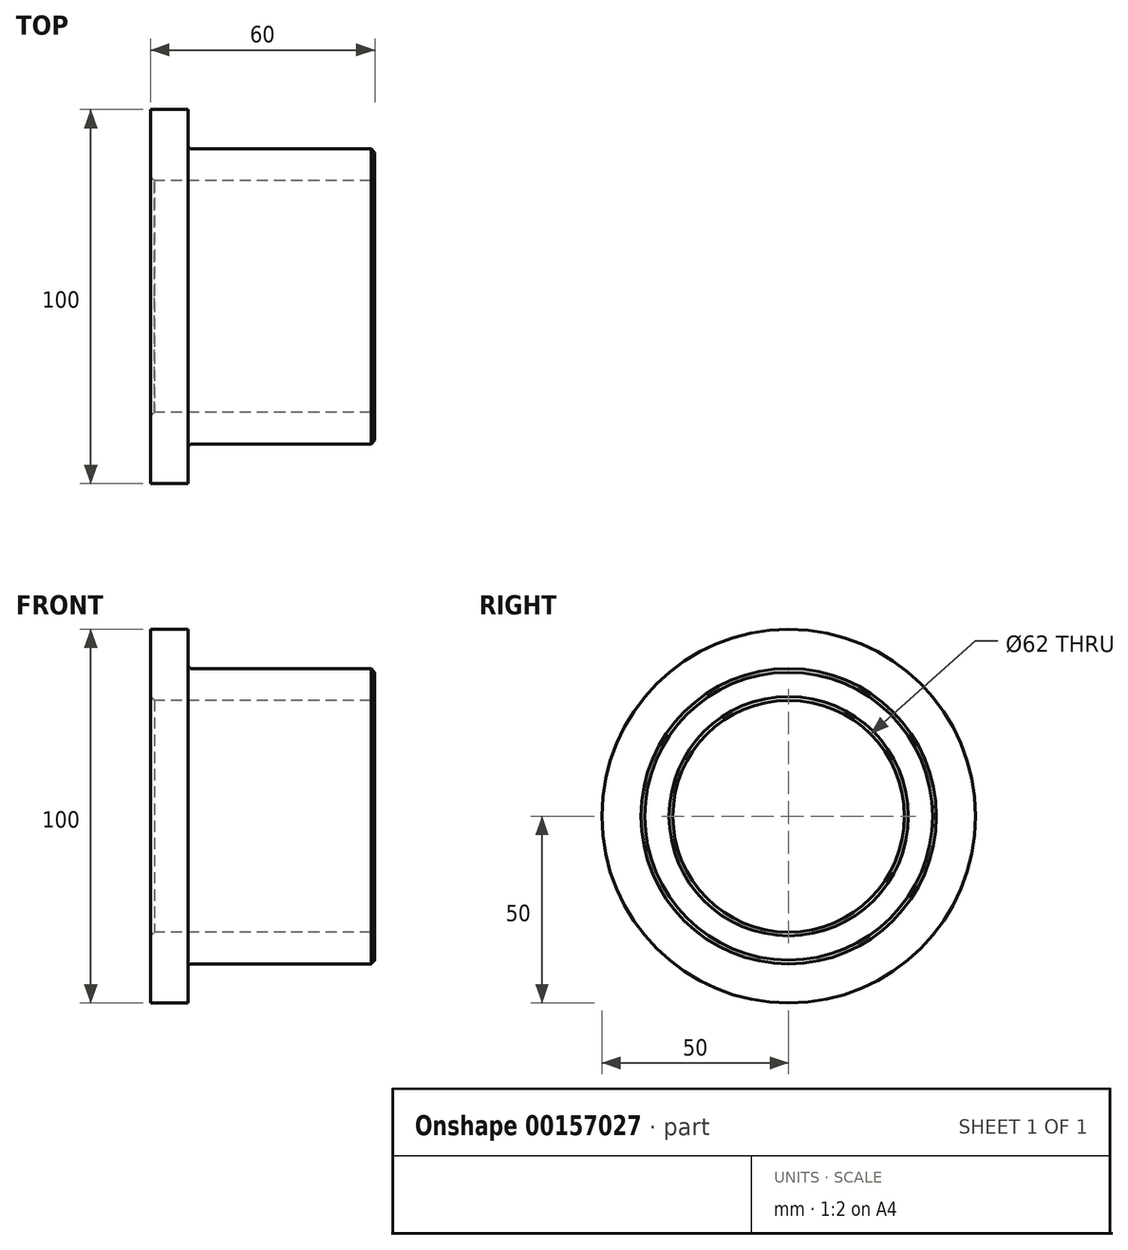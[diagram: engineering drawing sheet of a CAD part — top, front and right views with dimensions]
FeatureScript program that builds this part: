
annotation { "Feature Type Name" : "Feature", "Feature Type Description" : "" }
export const myFeature = defineFeature(function(context is Context, id is Id, definition is map)
    precondition{}
    {
        {
            var Q0;
            Q0=qCreatedBy(makeId("Front.planeOp"),FACE);
            var sketch = newSketch(context, id + "F0", { "sketchPlane" : qUnion([Q0])});
            skLineSegment(sketch, "E0", {"start": v(-96.67, 4.9) * mm, "end": v(-96.67, 23.9) * mm});
            skLineSegment(sketch, "E1", {"start": v(-96.67, 23.9) * mm, "end": v(-86.67, 23.9) * mm});
            skLineSegment(sketch, "E2", {"start": v(-86.67, 23.9) * mm, "end": v(-86.67, 13.4) * mm});
            skLineSegment(sketch, "E3", {"start": v(-86.67, 13.4) * mm, "end": v(-36.67, 13.4) * mm});
            skLineSegment(sketch, "E4", {"start": v(-36.67, 13.4) * mm, "end": v(-36.67, 4.9) * mm});
            skLineSegment(sketch, "E5", {"start": v(-36.67, 4.9) * mm, "end": v(-96.67, 4.9) * mm});
            skLineSegment(sketch, "E6", {"start": v(-114.18, -26.1) * mm, "end": v(56.03, -26.1) * mm});
            skSolve(sketch);
        }
        {
            var Q0;
            Q0 = qSketchRegion(id + "F0", true);
            var Q1;
            Q1=sQuery(id+"F0.wireOp",EDGE,"E6");
            revolve(context, id + "F1", {"entities" : qUnion([Q0]), "axis" : qUnion([Q1]), "revolveType" : RevolveType.FULL});
        }
        {
            var Q0;
            Q0=makeQuery(id+"F1.opRevolve","SWEPT_FACE",FACE,{"disambiguationData":[OSD([sQuery(id+"F0.wireOp",EDGE,"E4")])]});
            var Q1;
            Q1=makeQuery(id+"F1.opRevolve","SWEPT_EDGE",EDGE,{"disambiguationData":[OSD([sQuery(id+"F0.wireOp",EDGE,"E0"),sQuery(id+"F0.wireOp",EDGE,"E5")])]});
            chamfer(context, id + "F2", {"entities" : qUnion([Q0, Q1]), "width" : 1 * mm, "tangentPropagation" : true});
        }
        {
            var Q0;
            Q0=makeQuery(id+"F1.opRevolve","SWEPT_EDGE",EDGE,{"disambiguationData":[OSD([sQuery(id+"F0.wireOp",EDGE,"E2"),sQuery(id+"F0.wireOp",EDGE,"E3")])]});
            fillet(context, id + "F3", {"entities" : qUnion([Q0]), "radius" : 1 * mm, "tangentPropagation" : true, "allowEdgeOverflow" : false});
        }
    });
